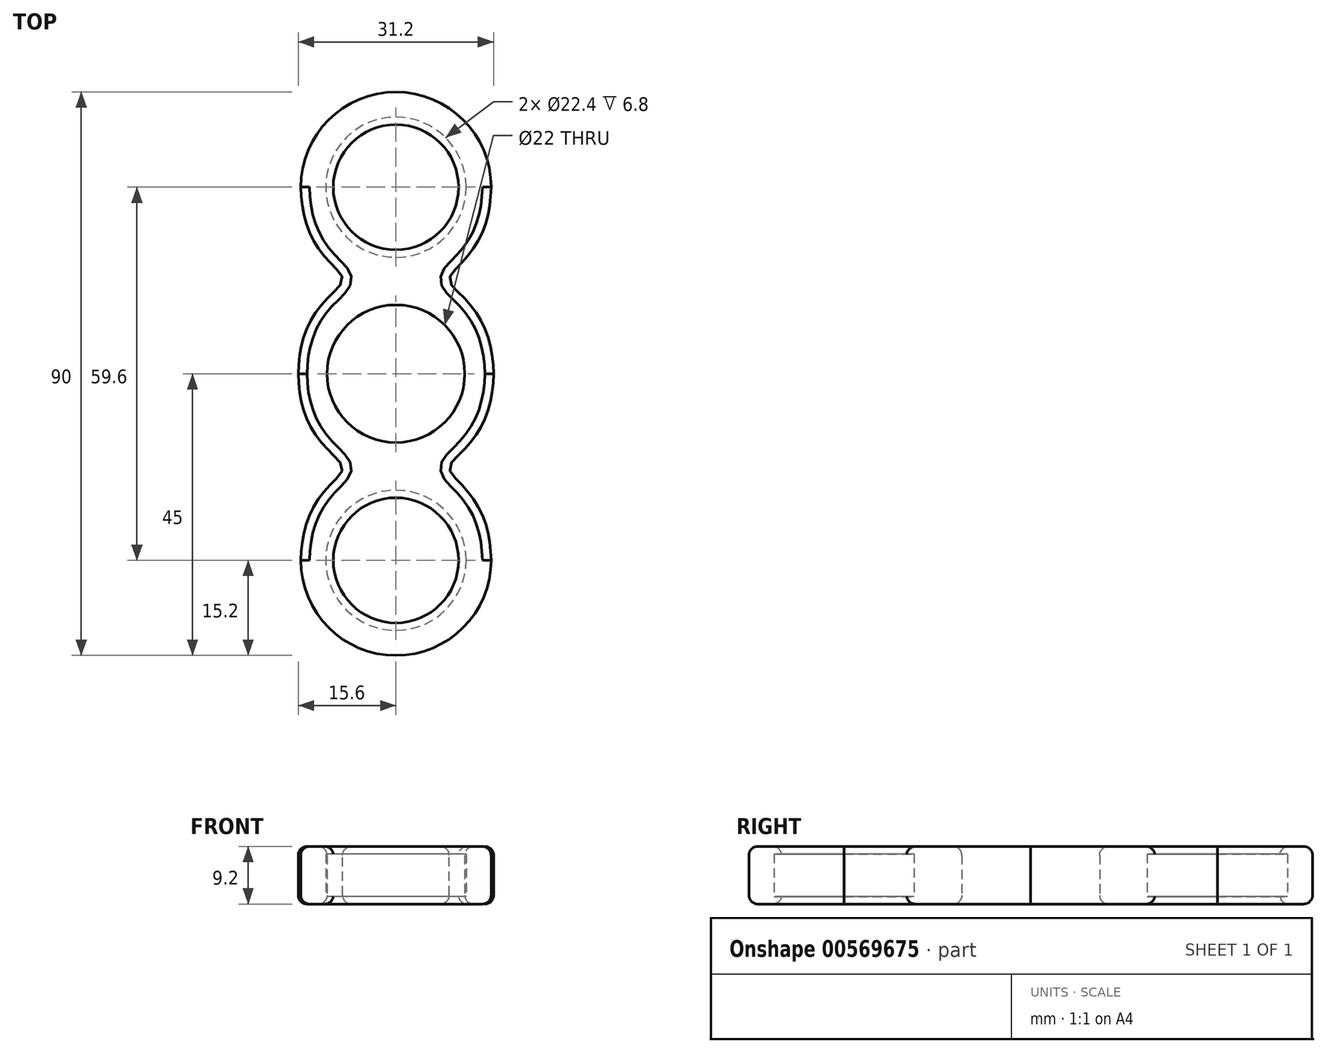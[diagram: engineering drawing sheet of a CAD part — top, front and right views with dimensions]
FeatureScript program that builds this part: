
annotation { "Feature Type Name" : "Feature", "Feature Type Description" : "" }
export const myFeature = defineFeature(function(context is Context, id is Id, definition is map)
    precondition{}
    {
        {
            var Q0;
            Q0=qCreatedBy(makeId("Top.planeOp"),FACE);
            var sketch = newSketch(context, id + "F0", { "sketchPlane" : qUnion([Q0])});
            skCircle(sketch, "E0", {"center": v(0, 0) * mm, "radius": 11 * mm});
            skFitSpline(sketch, "E1", {"points": [v(-15.6, 0) * mm, v(-8.5, 15.07) * mm, v(-15.2, 29.8) * mm], "startDerivative": vector(1.06, 64.71) * mm, "endDerivative": vector(-1.18, 64.87) * mm});
            skLineSegment(sketch, "E2", {"start": v(-41.07, 29.8) * mm, "end": v(58.78, 29.8) * mm, "construction": true});
            skArc(sketch, "E3", {"start": v(15.2, 29.8) * mm, "mid": v(0, 45) * mm, "end": v(-15.2, 29.8) * mm});
            skCircle(sketch, "E4", {"center": v(0, 29.8) * mm, "radius": 10 * mm});
            skFitSpline(sketch, "E5.MirrorCS", {"points": [v(15.6, 0) * mm, v(8.5, 15.07) * mm, v(15.2, 29.8) * mm], "startDerivative": vector(-1.06, 64.71) * mm, "endDerivative": vector(1.18, 64.87) * mm});
            skFitSpline(sketch, "E6.MirrorCS", {"points": [v(-15.6, 0) * mm, v(-8.5, -15.07) * mm, v(-15.2, -29.8) * mm], "startDerivative": vector(1.06, -64.71) * mm, "endDerivative": vector(-1.18, -64.87) * mm});
            skFitSpline(sketch, "E7.MirrorCS", {"points": [v(15.6, 0) * mm, v(8.5, -15.07) * mm, v(15.2, -29.8) * mm], "startDerivative": vector(-1.06, -64.71) * mm, "endDerivative": vector(1.18, -64.87) * mm});
            skArc(sketch, "E8.MirrorCS", {"start": v(15.2, -29.8) * mm, "mid": v(0, -45) * mm, "end": v(-15.2, -29.8) * mm});
            skCircle(sketch, "E9.MirrorC", {"center": v(0, -29.8) * mm, "radius": 10 * mm});
            skLineSegment(sketch, "E10", {"start": v(-8.5, 15.07) * mm, "end": v(8.5, 15.07) * mm, "construction": true});
            skSolve(sketch);
        }
        {
            var Q0;
            Q0 = qSketchRegion(id + "F0", true);
            extrude(context, id + "F1", {"entities" : qUnion([Q0]), "depth" : 9.2 * mm, "offsetDistance" : 25 * mm});
        }
        {
            var Q0;
            Q0=qCreatedBy(makeId("Top.planeOp"),FACE);
            cPlane(context, id + "F2", {"entities" : qUnion([Q0]), "cplaneType" : CPlaneType.OFFSET, "offset" : 1.2 * mm, "width" : 150 * mm, "height" : 150 * mm});
        }
        {
            var Q0;
            Q0=qCreatedBy(id+"F2.planeOp",FACE);
            var sketch = newSketch(context, id + "F3", { "sketchPlane" : qUnion([Q0])});
            skCircle(sketch, "E11", {"center": v(0, 29.8) * mm, "radius": 11.2 * mm});
            skCircle(sketch, "E12.MirrorC", {"center": v(0, -29.8) * mm, "radius": 11.2 * mm});
            skSolve(sketch);
        }
        {
            var Q0;
            Q0 = qSketchRegion(id + "F3", true);
            extrude(context, id + "F4", {"entities" : qUnion([Q0]), "operationType" : NewBodyOperationType.REMOVE, "depth" : 6.8 * mm, "offsetDistance" : 25 * mm});
        }
        {
            var Q0;
            Q0=makeQuery(id+"F1.opExtrude","CAP_FACE",FACE,{"disambiguationData":[OSD([sQuery(id+"F0.wireOp",EDGE,"E0"),sQuery(id+"F0.wireOp",EDGE,"E1"),sQuery(id+"F0.wireOp",EDGE,"E3"),sQuery(id+"F0.wireOp",EDGE,"YDB59UWS-9216-SCyM-1avY-P1zIQ8iXgfds"),sQuery(id+"F0.wireOp",EDGE,"E4"),sQuery(id+"F0.wireOp",EDGE,"E5.MirrorCS"),sQuery(id+"F0.wireOp",EDGE,"E6.MirrorCS"),sQuery(id+"F0.wireOp",EDGE,"E7.MirrorCS"),sQuery(id+"F0.wireOp",EDGE,"E8.MirrorCS"),sQuery(id+"F0.wireOp",EDGE,"E9.MirrorC"),sQuery(id+"F0.wireOp",EDGE,"a3595fab-1f4b-49de-854a-bb922f659e660.MirrorC")])],"isStart":false});
            var Q1;
            Q1=makeQuery(id+"F1.opExtrude","CAP_FACE",FACE,{"disambiguationData":[OSD([sQuery(id+"F0.wireOp",EDGE,"E0"),sQuery(id+"F0.wireOp",EDGE,"E1"),sQuery(id+"F0.wireOp",EDGE,"E3"),sQuery(id+"F0.wireOp",EDGE,"YDB59UWS-9216-SCyM-1avY-P1zIQ8iXgfds"),sQuery(id+"F0.wireOp",EDGE,"E4"),sQuery(id+"F0.wireOp",EDGE,"E5.MirrorCS"),sQuery(id+"F0.wireOp",EDGE,"E6.MirrorCS"),sQuery(id+"F0.wireOp",EDGE,"E7.MirrorCS"),sQuery(id+"F0.wireOp",EDGE,"E8.MirrorCS"),sQuery(id+"F0.wireOp",EDGE,"E9.MirrorC"),sQuery(id+"F0.wireOp",EDGE,"a3595fab-1f4b-49de-854a-bb922f659e660.MirrorC")])],"isStart":true});
            fillet(context, id + "F5", {"entities" : qUnion([Q0, Q1]), "radius" : 1.4 * mm, "tangentPropagation" : true, "allowEdgeOverflow" : false});
        }
    });
